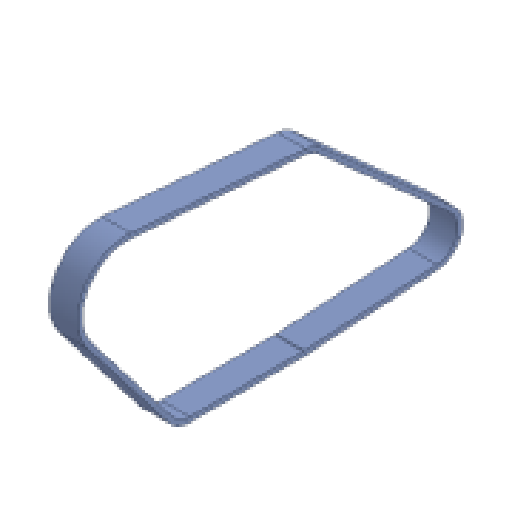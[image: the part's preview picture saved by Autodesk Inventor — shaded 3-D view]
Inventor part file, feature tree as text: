
AUTODESK INVENTOR PART (.ipt)
format: ipt  version: 2025 (Build 290162000, 162)  size: 118,784 bytes
history: native  units: in
note: dims shown in document units (in); Inventor stores cm internally (conversion verified against a paired STEP export)
features: extrude x1, sketch x1
ambient origin geometry x8: Origin, YZ Plane, XZ Plane, XY Plane, X Axis, Y Axis, Z Axis, Center Point
bodies: Solid1 (feature_tree)
feature tree (2):
  extrude  "Extrusion1"  Depth=3.125in
  sketch  "Sketch1"  dims[d0=6.25in d1=3.125in d2=3.125in d3=3.125in d4=3.125in d6=20.5in d7=8.0in d8=2.0in d9=0.0in]
